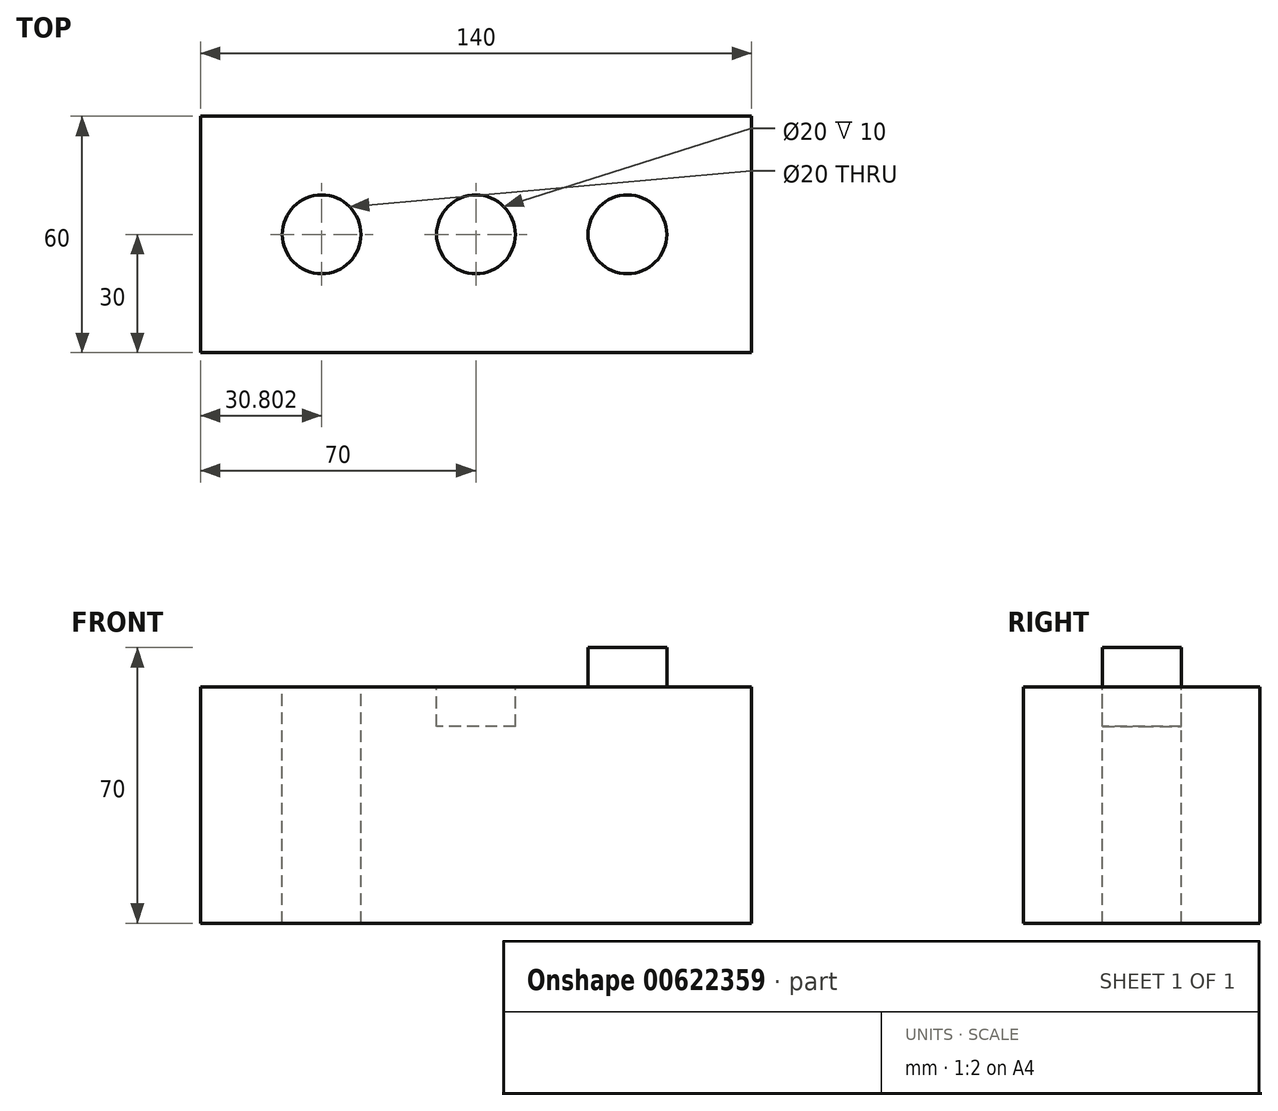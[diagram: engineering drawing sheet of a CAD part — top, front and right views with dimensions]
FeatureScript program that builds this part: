
annotation { "Feature Type Name" : "Feature", "Feature Type Description" : "" }
export const myFeature = defineFeature(function(context is Context, id is Id, definition is map)
    precondition{}
    {
        {
            var Q0;
            Q0=qCreatedBy(makeId("Top.planeOp"),FACE);
            var sketch = newSketch(context, id + "F0", { "sketchPlane" : qUnion([Q0])});
            skLineSegment(sketch, "E0.bottom", {"start": v(-70, -30) * mm, "end": v(70, -30) * mm});
            skLineSegment(sketch, "E0.top", {"start": v(-70, 30) * mm, "end": v(70, 30) * mm});
            skLineSegment(sketch, "E0.left", {"start": v(-70, -30) * mm, "end": v(-70, 30) * mm});
            skLineSegment(sketch, "E0.right", {"start": v(70, -30) * mm, "end": v(70, 30) * mm});
            skPoint(sketch, "E0.middle", {"position": v(0, 0) * mm});
            skSolve(sketch);
        }
        {
            var Q0;
            Q0 = qSketchRegion(id + "F0", true);
            extrude(context, id + "F1", {"entities" : qUnion([Q0]), "depth" : 60 * mm, "offsetDistance" : 25 * mm});
        }
        {
            var Q0;
            Q0=makeQuery(id+"F1.opExtrude","CAP_FACE",FACE,{"disambiguationData":[OSD([sQuery(id+"F0.wireOp",EDGE,"E0.bottom"),sQuery(id+"F0.wireOp",EDGE,"E0.top"),sQuery(id+"F0.wireOp",EDGE,"E0.left"),sQuery(id+"F0.wireOp",EDGE,"E0.right")])],"isStart":false});
            var sketch = newSketch(context, id + "F2", { "sketchPlane" : qUnion([Q0])});
            skCircle(sketch, "E1", {"center": v(0, 0) * mm, "radius": 10 * mm});
            skSolve(sketch);
        }
        {
            var Q0;
            Q0 = qSketchRegion(id + "F2", true);
            extrude(context, id + "F3", {"entities" : qUnion([Q0]), "operationType" : NewBodyOperationType.REMOVE, "oppositeDirection" : true, "depth" : 10 * mm, "offsetDistance" : 25 * mm});
        }
        {
            var Q0;
            Q0=makeQuery(id+"F1.opExtrude","CAP_FACE",FACE,{"disambiguationData":[OSD([sQuery(id+"F0.wireOp",EDGE,"E0.bottom"),sQuery(id+"F0.wireOp",EDGE,"E0.top"),sQuery(id+"F0.wireOp",EDGE,"E0.left"),sQuery(id+"F0.wireOp",EDGE,"E0.right")])],"isStart":false});
            var sketch = newSketch(context, id + "F4", { "sketchPlane" : qUnion([Q0])});
            skLineSegment(sketch, "E2", {"start": v(-10, 0) * mm, "end": v(-30, 0) * mm});
            skSolve(sketch);
        }
        {
            var Q0;
            Q0=makeQuery(id+"F4.imprint","IMPRINT",FACE,{"disambiguationData":[TD([[makeQuery(id+"F4.imprint","IMPRINT",EDGE,{"derivedFrom":makeQuery(id+"F1.opExtrude","CAP_EDGE",EDGE,{"disambiguationData":[OSD([sQuery(id+"F0.wireOp",EDGE,"E0.bottom")])],"isStart":false})}),1.0]])]});
            var sketch = newSketch(context, id + "F5", { "sketchPlane" : qUnion([Q0])});
            skCircle(sketch, "E3", {"center": v(-39.2, 0) * mm, "radius": 10 * mm});
            skSolve(sketch);
        }
        {
            var Q0;
            Q0 = qSketchRegion(id + "F5", true);
            extrude(context, id + "F6", {"entities" : qUnion([Q0]), "operationType" : NewBodyOperationType.REMOVE, "oppositeDirection" : true, "depth" : 77.4 * mm, "offsetDistance" : 25 * mm});
        }
        {
            var Q0;
            Q0=makeQuery(id+"F4.imprint","IMPRINT",FACE,{"disambiguationData":[TD([[makeQuery(id+"F4.imprint","IMPRINT",EDGE,{"derivedFrom":makeQuery(id+"F1.opExtrude","CAP_EDGE",EDGE,{"disambiguationData":[OSD([sQuery(id+"F0.wireOp",EDGE,"E0.bottom")])],"isStart":false})}),1.0]])]});
            var sketch = newSketch(context, id + "F7", { "sketchPlane" : qUnion([Q0])});
            skCircle(sketch, "E4", {"center": v(38.49, 0) * mm, "radius": 10 * mm});
            skSolve(sketch);
        }
        {
            var Q0;
            Q0 = qSketchRegion(id + "F7", true);
            extrude(context, id + "F8", {"entities" : qUnion([Q0]), "operationType" : NewBodyOperationType.ADD, "depth" : 10 * mm, "offsetDistance" : 25 * mm});
        }
    });
